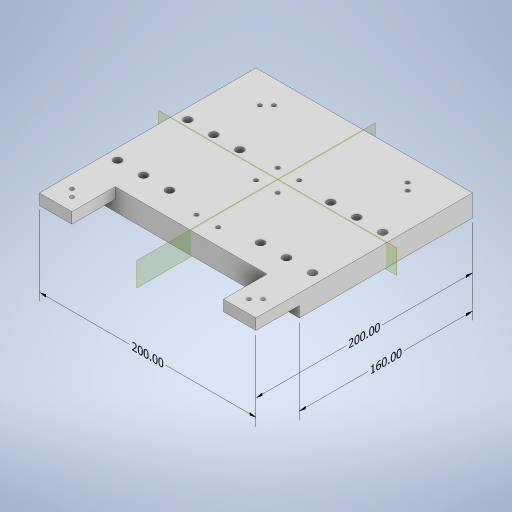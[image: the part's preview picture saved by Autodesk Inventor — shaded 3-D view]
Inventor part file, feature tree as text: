
AUTODESK INVENTOR PART (.ipt)
format: ipt  version: 2023 (Build 270158000, 158)  size: 373,248 bytes
history: native  units: mm
features: sketch x8, other x5, extrude x5, hole x3, plane x2
ambient origin geometry x8: Origin, YZ Plane, XZ Plane, XY Plane, X Axis, Y Axis, Z Axis, Center Point
bodies: Body1 (feature_tree)
feature tree (23):
  other  "Sólido1"
  other  "Anotaciones"
  extrude  "Extrusión1"  Depth=160.0mm
  extrude  "Extrusión2"  TaperAngle=0.0deg  [1 undecoded]
  extrude  "Extrusión3"  Depth=20.0mm TaperAngle=0.0deg
  extrude  "Extrusión4"  Depth=10.0mm
  hole  "Agujero1"  [1 undecoded]
  plane  "Plano de trabajo1"
  plane  "Plano de trabajo2"
  hole  "Agujero2"  [1 undecoded]
  extrude  "Extrusión5"  Depth=10.0mm
  hole  "Agujero3"  [1 undecoded]
  sketch  "Boceto1"  dims[d0=200.0mm d1=160.0mm]
  sketch  "Boceto2"  dims[d2=20.0mm d3=0.0mm]
  sketch  "Boceto3"  dims[d4=7.0mm d5=68.0mm d6=80.0mm d7=7.6mm d8=10.0mm d9=7.0mm d10=24.0mm d11=10.0mm d16=0.0mm]
  sketch  "Boceto4"  dims[d19=40.0mm d20=20.0mm d21=0.0mm]
  sketch  "Boceto5"  dims[d22=30.0mm d23=10.0mm]
  sketch  "Boceto6"  dims[d24=40.0mm d25=0.0mm d26=1.75mm]
  sketch  "Boceto7"  dims[d27=8.25mm d28=20.0mm]
  sketch  "Boceto8"  dims[d29=10.0mm d30=10.0mm d31=1.75mm d32=1.75mm d33=1.75mm d34=40.0mm d35=0.0mm d36=11.749873mm d37=40.0mm d38=29.999873mm d39=21.75mm d40=11.75mm d41=28.300341mm d42=11.749873mm d43=0.0mm d44=0.0mm d45=3.5mm d46=6.0mm d47=4.0mm d48=2.0mm d49=90.0deg d50=8.0mm d51=20.594885mm d58=30.0mm d59=30.0mm d63=3.5mm d64=10.0mm d65=10.0mm d66=3.5mm d67=6.0mm d68=4.0mm d69=2.0mm d70=90.0deg d71=8.0mm d72=20.594885mm d73=32.0mm d74=32.0mm d75=10.0mm d76=0.0mm d77=10.0mm d78=30.0mm d79=5.0mm d80=5.0mm d81=5.0mm d82=5.0mm d83=3.5mm d84=6.0mm d85=4.0mm d86=2.0mm d87=90.0deg d88=8.0mm d89=20.594885mm d52=6.692993mm d53=5.009025mm d54=200.0mm d55=6.065637mm d56=3.288093mm d57=200.0mm d60=3.204885mm d61=4.144173mm d62=160.0mm]
  other  "Cota lineal 1"
  other  "Cota lineal 2"
  other  "Cota lineal 3"
note: 4 required parameter values undecoded (feature->parameter linkage not recoverable at this tier; creation-order binding heuristic only, values carry confidence <= 0.55)
